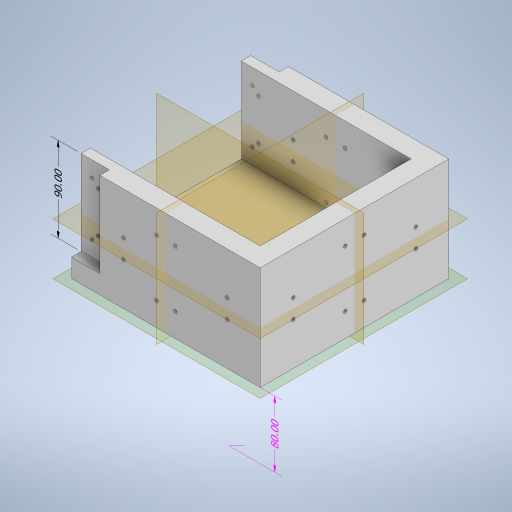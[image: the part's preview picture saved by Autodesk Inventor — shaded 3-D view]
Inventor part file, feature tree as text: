
AUTODESK INVENTOR PART (.ipt)
format: ipt  version: 2023 (Build 270158000, 158)  size: 424,448 bytes
history: native  units: mm
features: sketch x9, extrude x5, other x4, hole x4, plane x4, split x1
ambient origin geometry x8: Origin, YZ Plane, XZ Plane, XY Plane, X Axis, Y Axis, Z Axis, Center Point
bodies: Body1 (feature_tree)
feature tree (27):
  other  "Sólido1"
  other  "Anotaciones"
  extrude  "Extrusión1"  Depth=200.0mm
  hole  "Agujero1"  [1 undecoded]
  extrude  "Extrusión2"  Depth=15.0mm
  extrude  "Extrusión3"  Depth=20.0mm TaperAngle=0.0deg
  extrude  "Extrusión4"  Depth=200.0mm
  extrude  "Extrusión5"  Depth=20.0mm
  hole  "Agujero2"  [1 undecoded]
  plane  "Plano de trabajo1"
  split  "Dividir1"
  plane  "Plano de trabajo2"
  plane  "Plano de trabajo3"
  sketch  "Boceto9"  dims[d37=20.0mm d38=20.0mm]
  plane  "Plano de trabajo4"
  hole  "Agujero3"  [1 undecoded]
  hole  "Agujero4"  [1 undecoded]
  sketch  "Boceto2"  dims[d7=15.0mm d8=200.0mm]
  sketch  "Boceto3"  dims[d9=10.0mm d10=0.0mm]
  sketch  "Boceto4"  dims[d12=1.75mm d13=1.75mm d14=1.75mm d15=1.75mm d16=10.0mm d17=10.0mm d19=30.0mm]
  sketch  "Boceto5"  dims[d20=3.5mm d21=6.0mm d22=4.0mm d23=2.0mm d24=90.0deg d25=8.0mm d26=20.594885mm d27=15.0mm]
  sketch  "Boceto6"  dims[d28=20.0mm d29=80.0mm d30=0.0mm]
  sketch  "Boceto7"  dims[d31=48.0mm d32=200.0mm]
  sketch  "Boceto8"  dims[d33=110.0mm d34=0.0mm d36=20.0mm]
  sketch  "Boceto10"  dims[d39=90.0mm d40=0.0mm d42=10.0mm d43=30.0mm d44=0.0mm d46=1.75mm d47=1.75mm d48=1.75mm d49=1.75mm d50=10.0mm d51=10.0mm d52=15.0mm d56=3.5mm d57=6.0mm d58=4.0mm d59=2.0mm d60=90.0deg d61=8.0mm d62=20.594885mm d63=10.0mm d65=10.0mm d66=10.0mm d67=31.75mm d70=15.0mm d74=200.0mm d78=20.0mm d82=90.0deg d83=10.0mm d84=30.0mm d85=5.0mm d86=5.0mm d87=5.0mm d88=5.0mm d89=20.0mm d91=30.0mm d92=5.0mm d93=5.0mm d94=3.5mm d95=5.0mm d96=5.0mm d97=5.0mm d98=5.0mm d99=5.0mm d100=20.0mm d101=3.5mm d102=6.0mm d103=4.0mm d104=2.0mm d105=90.0deg d106=8.0mm d107=20.594885mm d108=10.0mm d109=30.0mm d110=5.0mm d111=5.0mm d112=5.0mm d113=5.0mm d114=5.0mm d115=5.0mm d116=3.5mm d117=5.0mm d118=5.0mm d119=5.0mm d120=5.0mm d121=5.0mm d122=30.0mm d123=30.0mm d124=3.5mm d125=6.0mm d126=4.0mm d127=2.0mm d128=90.0deg d129=8.0mm d130=20.594885mm d75=1.454734mm d76=6.982969mm d77=80.0mm d79=4.097996mm d80=1.406125mm d81=90.0mm]
  other  "Cota lineal 2"
  other  "Cota lineal 3"
note: 4 required parameter values undecoded (feature->parameter linkage not recoverable at this tier; creation-order binding heuristic only, values carry confidence <= 0.55)
